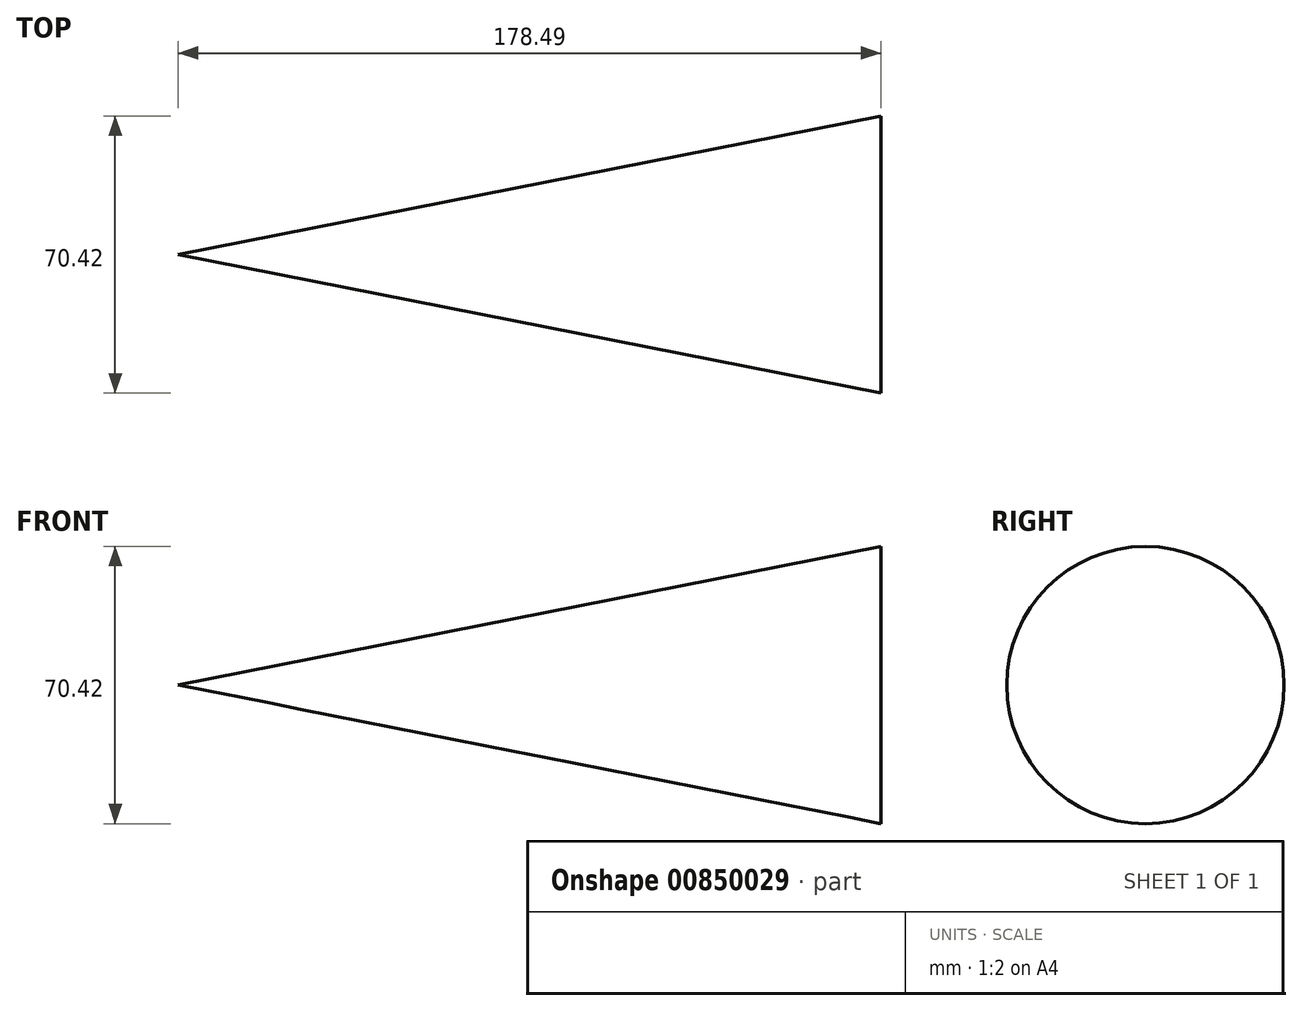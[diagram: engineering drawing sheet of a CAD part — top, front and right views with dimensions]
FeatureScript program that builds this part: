
annotation { "Feature Type Name" : "Feature", "Feature Type Description" : "" }
export const myFeature = defineFeature(function(context is Context, id is Id, definition is map)
    precondition{}
    {
        {
            var Q0;
            Q0=qCreatedBy(makeId("Top.planeOp"),FACE);
            var sketch = newSketch(context, id + "F0", { "sketchPlane" : qUnion([Q0])});
            skLineSegment(sketch, "E0", {"start": v(-88.9, 0) * mm, "end": v(88.9, 0) * mm});
            skLineSegment(sketch, "E1", {"start": v(0, -34.93) * mm, "end": v(0, 34.93) * mm});
            skSolve(sketch);
        }
        {
            var Q0;
            Q0=qCreatedBy(makeId("Top.planeOp"),FACE);
            var Q1;
            Q1=qCreatedBy(makeId("Top.planeOp"),FACE);
            var sketch = newSketch(context, id + "F1", { "sketchPlane" : qUnion([Q0, Q1])});
            skLineSegment(sketch, "E2", {"start": v(88.9, -35.2) * mm, "end": v(88.9, 0) * mm});
            skLineSegment(sketch, "E3", {"start": v(-89.59, 0) * mm, "end": v(88.9, -35.2) * mm});
            skSolve(sketch);
        }
        {
            var Q0;
            Q0=sQuery(id+"F1.wireOp",EDGE,"E3");
            var Q1;
            Q1=sQuery(id+"F1.wireOp",EDGE,"E2");
            var Q2;
            Q2=sQuery(id+"F1.wireOp",EDGE,"E3");
            var Q3;
            Q3=sQuery(id+"F1.wireOp",EDGE,"E2");
            var Q4;
            Q4=sQuery(id+"F0.wireOp",EDGE,"E0");
            revolve(context, id + "F2", {"bodyType" : ToolBodyType.SURFACE, "surfaceOperationType" : NewSurfaceOperationType.NEW, "surfaceEntities" : qUnion([Q0, Q1, Q2, Q3]), "axis" : qUnion([Q4]), "revolveType" : RevolveType.FULL});
        }
    });
